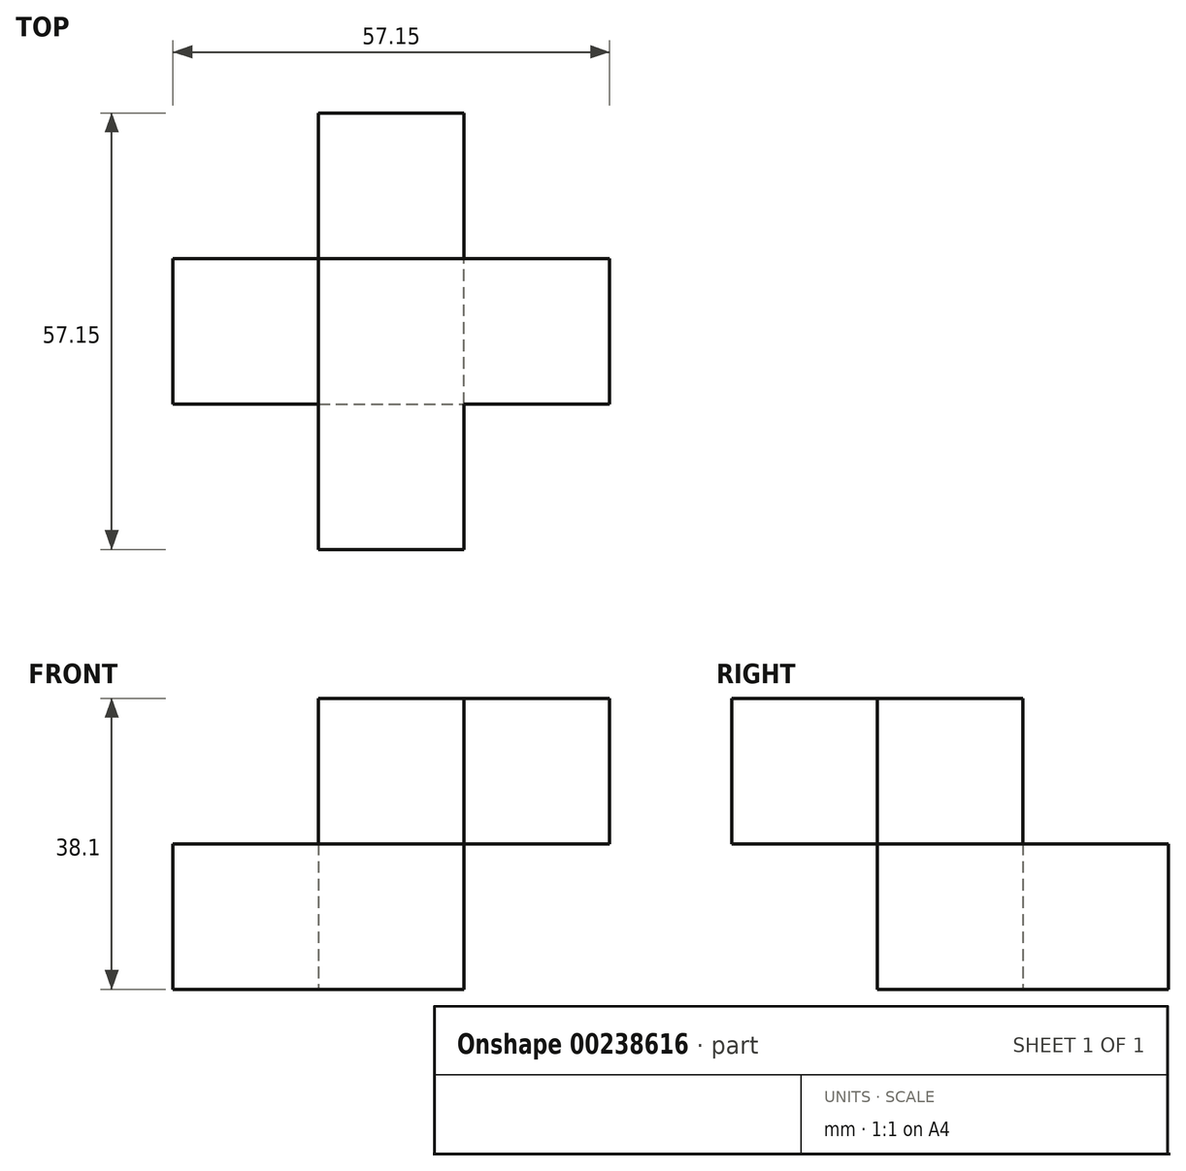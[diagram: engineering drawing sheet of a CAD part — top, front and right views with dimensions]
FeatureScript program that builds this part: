
annotation { "Feature Type Name" : "Feature", "Feature Type Description" : "" }
export const myFeature = defineFeature(function(context is Context, id is Id, definition is map)
    precondition{}
    {
        {
            var Q0;
            Q0=qCreatedBy(makeId("Top.planeOp"),FACE);
            var sketch = newSketch(context, id + "F0", { "sketchPlane" : qUnion([Q0])});
            skLineSegment(sketch, "E0", {"start": v(0, 0) * mm, "end": v(-19.05, 0) * mm});
            skLineSegment(sketch, "E1", {"start": v(-19.05, 0) * mm, "end": v(-19.05, -19.05) * mm});
            skLineSegment(sketch, "E2", {"start": v(-19.05, -19.05) * mm, "end": v(19.05, -19.05) * mm});
            skLineSegment(sketch, "E3", {"start": v(19.05, -19.05) * mm, "end": v(19.05, 19.05) * mm});
            skLineSegment(sketch, "E4", {"start": v(19.05, 19.05) * mm, "end": v(0, 19.05) * mm});
            skLineSegment(sketch, "E5", {"start": v(0, 19.05) * mm, "end": v(0, 0) * mm});
            skSolve(sketch);
        }
        {
            var Q0;
            Q0 = qSketchRegion(id + "F0", true);
            extrude(context, id + "F1", {"entities" : qUnion([Q0]), "depth" : 19.05 * mm});
        }
        {
            var Q0;
            Q0=makeQuery(id+"F1.opExtrude","CAP_FACE",FACE,{"disambiguationData":[OSD([sQuery(id+"F0.wireOp",EDGE,"E0"),sQuery(id+"F0.wireOp",EDGE,"E1"),sQuery(id+"F0.wireOp",EDGE,"E2"),sQuery(id+"F0.wireOp",EDGE,"E3"),sQuery(id+"F0.wireOp",EDGE,"E4"),sQuery(id+"F0.wireOp",EDGE,"E5")])],"isStart":false});
            var sketch = newSketch(context, id + "F2", { "sketchPlane" : qUnion([Q0])});
            skLineSegment(sketch, "E6", {"start": v(0, 0) * mm, "end": v(0, -19.05) * mm});
            skLineSegment(sketch, "E7", {"start": v(0, -19.05) * mm, "end": v(0, -38.1) * mm});
            skLineSegment(sketch, "E8", {"start": v(0, -38.1) * mm, "end": v(19.05, -38.1) * mm});
            skLineSegment(sketch, "E9", {"start": v(19.05, -38.1) * mm, "end": v(19.05, -19.05) * mm});
            skLineSegment(sketch, "E10", {"start": v(19.05, -19.05) * mm, "end": v(38.1, -19.05) * mm});
            skLineSegment(sketch, "E11", {"start": v(38.1, -19.05) * mm, "end": v(38.1, 0) * mm});
            skLineSegment(sketch, "E12", {"start": v(38.1, 0) * mm, "end": v(0, 0) * mm});
            skSolve(sketch);
        }
        {
            var Q0;
            Q0 = qSketchRegion(id + "F2", true);
            extrude(context, id + "F3", {"entities" : qUnion([Q0]), "operationType" : NewBodyOperationType.ADD, "depth" : 19.05 * mm});
        }
    });
